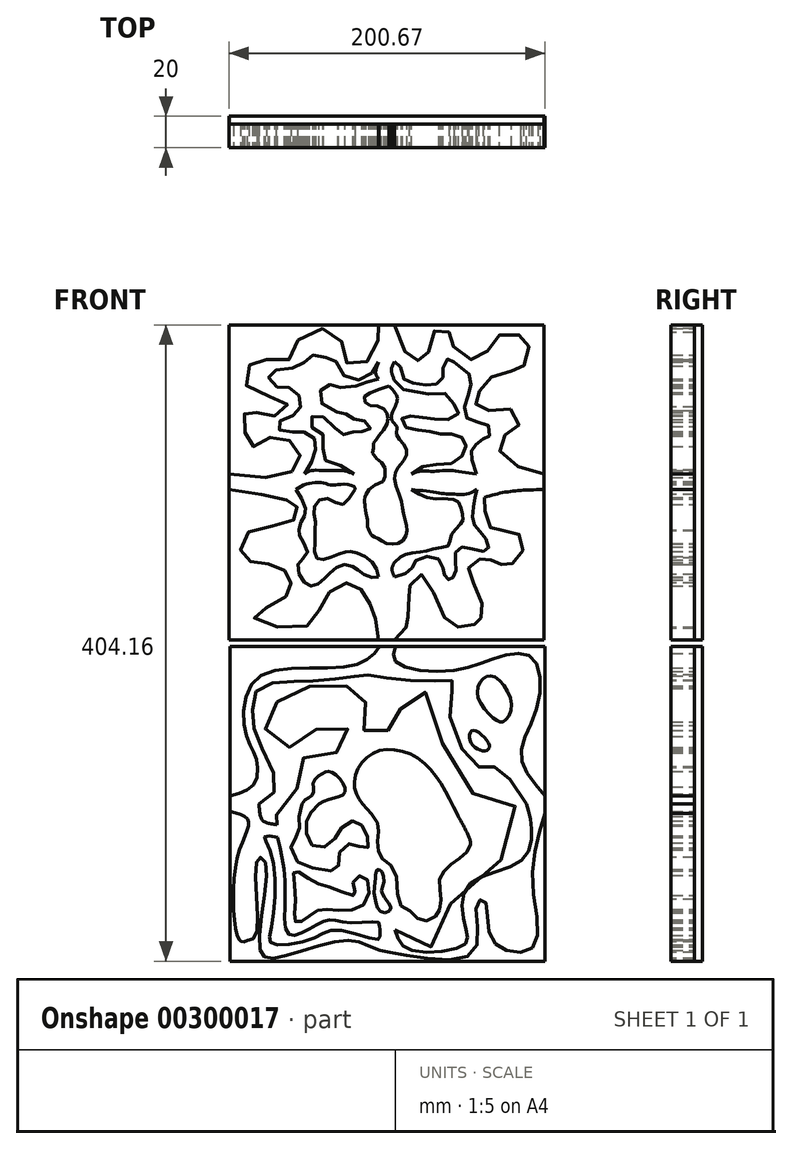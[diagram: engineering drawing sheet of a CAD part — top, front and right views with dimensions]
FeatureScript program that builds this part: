
annotation { "Feature Type Name" : "Feature", "Feature Type Description" : "" }
export const myFeature = defineFeature(function(context is Context, id is Id, definition is map)
    precondition{}
    {
        {
            var Q0;
            Q0=qCreatedBy(makeId("Front.planeOp"),FACE);
            var sketch = newSketch(context, id + "F0", { "sketchPlane" : qUnion([Q0])});
            skLineSegment(sketch, "E0", {"start": v(-68.5, 100) * mm, "end": v(-68.5, 5) * mm});
            skLineSegment(sketch, "E1", {"start": v(-33.6, 0) * mm, "end": v(31.5, 0) * mm});
            skLineSegment(sketch, "E2.MirrorCS", {"start": v(-33.6, 0) * mm, "end": v(-33.6, -5) * mm});
            skLineSegment(sketch, "E3.trimOffspring", {"start": v(-68.5, -5) * mm, "end": v(-68.5, -100) * mm});
            skPoint(sketch, "E4.orphan", {"position": v(-68.5, 0) * mm});
            skPoint(sketch, "E5.end.orphan", {"position": v(-33.6, 5) * mm});
            skPoint(sketch, "E5.start.orphan", {"position": v(-33.6, 0) * mm});
            skPoint(sketch, "E6.orphan", {"position": v(131.5, 0) * mm});
            skLineSegment(sketch, "E7.MirrorCS", {"start": v(131.5, 100) * mm, "end": v(131.5, 5) * mm});
            skLineSegment(sketch, "E8.MirrorCS", {"start": v(131.5, -6.17) * mm, "end": v(131.5, -101.16) * mm});
            skFitSpline(sketch, "E9", {"points": [v(-68.5, -5) * mm, v(-56.9, -10.75) * mm, v(-63.65, -33.28) * mm, v(-62.81, -86.22) * mm, v(-57.46, -86.78) * mm], "startDerivative": vector(80.53, -15.15) * mm, "endDerivative": vector(58.49, 27.23) * mm});
            skFitSpline(sketch, "E10", {"points": [v(-57.46, -86.78) * mm, v(-51.83, -82.56) * mm, v(-50.98, -34.96) * mm, v(-46.2, -36.94) * mm, v(-49.57, -92.42) * mm, v(-38.6, -97.77) * mm, v(5.06, -86.78) * mm, v(26.6, -93.16) * mm], "startDerivative": vector(88.86, 11.23) * mm, "endDerivative": vector(182.3, -63.3) * mm});
            skFitSpline(sketch, "E11", {"points": [v(26.6, -93.16) * mm, v(50.85, -97.41) * mm, v(87.45, -92.35) * mm, v(88.43, -62.85) * mm, v(93.18, -61.47) * mm, v(96.03, -81.43) * mm, v(108.14, -93.53) * mm, v(125.01, -89.87) * mm, v(123.62, -49.6) * mm, v(131.5, -6.17) * mm], "startDerivative": vector(93.77, -18.16) * mm, "endDerivative": vector(84.11, 264.75) * mm});
            skPoint(sketch, "E12.orphan", {"position": v(131.5, 101.16) * mm});
            skPoint(sketch, "E13.start.orphan", {"position": v(31.5, 100.58) * mm});
            skPoint(sketch, "E14.MirrorCS.end.orphan", {"position": v(31.5, -201.16) * mm});
            skPoint(sketch, "E14.MirrorCS.start.orphan", {"position": v(-33.6, -201.16) * mm});
            skLineSegment(sketch, "E15", {"start": v(-68.5, 100) * mm, "end": v(26.5, 100) * mm});
            skLineSegment(sketch, "E16", {"start": v(131.5, 100) * mm, "end": v(36.5, 100) * mm});
            skFitSpline(sketch, "E17", {"points": [v(-68.5, 5) * mm, v(-53.5, 12.19) * mm, v(-52.02, 28.9) * mm, v(-58.28, 43.81) * mm, v(-51.12, 79.92) * mm, v(7.66, 87.37) * mm, v(26.5, 100) * mm], "startDerivative": vector(131.47, 41.7) * mm, "endDerivative": vector(63, 102.47) * mm});
            skFitSpline(sketch, "E18", {"points": [v(36.5, 100) * mm, v(36.5, 90.36) * mm, v(71.2, 84.4) * mm, v(100.75, 92.74) * mm, v(123.12, 93.04) * mm, v(126.4, 61.12) * mm, v(116.26, 30.39) * mm, v(131.5, 5) * mm], "startDerivative": vector(-36.62, -111.2) * mm, "endDerivative": vector(143.7, -169.43) * mm});
            skFitSpline(sketch, "E19", {"points": [v(-50.1, 0) * mm, v(-39.36, 11.13) * mm, v(-50.1, 38.63) * mm, v(-54.21, 56.33) * mm, v(-51.05, 72.45) * mm, v(-32.08, 77.5) * mm, v(-13.43, 78.14) * mm, v(8.7, 80.67) * mm, v(18.04, 81.83) * mm, v(36.5, 79.09) * mm, v(64.96, 78.14) * mm, v(73.5, 77.5) * mm, v(70.65, 62.33) * mm, v(88.35, 23.77) * mm, v(100.36, 23.14) * mm, v(119.65, 0) * mm], "startDerivative": vector(256.93, 149.04) * mm, "endDerivative": vector(237.27, -390.24) * mm});
            skFitSpline(sketch, "E20", {"points": [v(119.65, 0) * mm, v(122.67, -12.95) * mm, v(116.9, -35.78) * mm, v(82.78, -51.84) * mm, v(81.02, -78.94) * mm, v(80.52, -89.22) * mm, v(45.14, -92.48) * mm, v(36.36, -80.2) * mm], "startDerivative": vector(32.09, -102.65) * mm, "endDerivative": vector(-34.37, 125.86) * mm});
            skFitSpline(sketch, "E21", {"points": [v(-50.1, 0) * mm, v(-47.69, -10.75) * mm, v(-38.66, -13.3) * mm], "startDerivative": vector(1.1, -24.27) * mm, "endDerivative": vector(22, -4.45) * mm});
            skFitSpline(sketch, "E22", {"points": [v(-38.4, -21.23) * mm, v(-46.43, -20.98) * mm, v(-41.67, -33.78) * mm, v(-42.67, -80.2) * mm, v(-41.92, -88.72) * mm, v(-15.57, -85.46) * mm, v(0, -80.2) * mm, v(26.5, -85.96) * mm, v(26.58, -80.2) * mm], "startDerivative": vector(-126.45, 23) * mm, "endDerivative": vector(39.4, 95.48) * mm});
            skFitSpline(sketch, "E23", {"points": [v(26.58, -80.2) * mm, v(26.5, -75.87) * mm, v(7.13, -75.58) * mm, v(-5.7, -73.79) * mm, v(-19.12, -80.2) * mm, v(-31.36, -82.74) * mm, v(-33.45, -53.8) * mm, v(-38.4, -21.23) * mm], "startDerivative": vector(-44.26, 59.3) * mm, "endDerivative": vector(-36.17, 149.66) * mm});
            skFitSpline(sketch, "E24", {"points": [v(-12.86, -67.82) * mm, v(-22.1, -74.38) * mm, v(-27.18, -74.68) * mm, v(-26.88, -60.66) * mm, v(-27.48, -42.76) * mm, v(-17.33, -48.42) * mm, v(-3.01, -53.8) * mm, v(11.01, -57.97) * mm, v(9.52, -50.21) * mm, v(16.68, -46.04) * mm, v(17.87, -62.45) * mm, v(0, -67.82) * mm, v(-12.86, -67.82) * mm]});
            skFitSpline(sketch, "E25", {"points": [v(92.17, 79.28) * mm, v(100.22, 80.17) * mm, v(110.37, 62.27) * mm, v(105, 52.12) * mm, v(99.92, 53.62) * mm, v(88.88, 67.94) * mm, v(92.17, 79.28) * mm]});
            skFitSpline(sketch, "E26", {"points": [v(93.36, 33.63) * mm, v(84.26, 39.3) * mm, v(85.6, 46.46) * mm, v(96.05, 37.5) * mm, v(93.36, 33.63) * mm]});
            skFitSpline(sketch, "E27", {"points": [v(-38.66, -13.3) * mm, v(-33.46, -13.3) * mm, v(-31.83, -8.37) * mm, v(-38.66, -8.02) * mm, v(-38.66, -5) * mm, v(-35.99, 5) * mm, v(-28.3, 9.03) * mm, v(-23.95, 10.94) * mm, v(-22.59, 18.28) * mm, v(-23.68, 27.25) * mm, v(-18.78, 30.5) * mm, v(-12.26, 32.96) * mm, v(-4.1, 32.96) * mm, v(2.7, 32.68) * mm, v(10.58, 38.94) * mm, v(8.13, 46) * mm, v(0, 49.54) * mm, v(-5.73, 49.54) * mm, v(-12.26, 48.18) * mm, v(-15.8, 46) * mm, v(-21.5, 41.93) * mm, v(-27.48, 36.22) * mm, v(-33.6, 36.57) * mm, v(-38.66, 39.01) * mm, v(-44.07, 42.47) * mm, v(-46.2, 48.73) * mm, v(-46.2, 52.53) * mm, v(-46.2, 58.51) * mm, v(-38.66, 64.57) * mm, v(-35.99, 66.7) * mm, v(-30.47, 72.92) * mm, v(-16.6, 74.28) * mm, v(-6, 73.2) * mm, v(0, 74.55) * mm, v(8.4, 74.55) * mm, v(14.66, 73.2) * mm, v(16.83, 71.02) * mm, v(17.65, 65.3) * mm, v(16.02, 59.33) * mm, v(15.2, 54.98) * mm, v(15.47, 50.9) * mm, v(17.1, 45.2) * mm, v(18.2, 43.02) * mm, v(22.81, 43.29) * mm, v(28.52, 45.2) * mm, v(35.05, 48.18) * mm, v(37.77, 49.54) * mm, v(41.03, 54.98) * mm, v(39.94, 59.87) * mm, v(37.77, 69.12) * mm, v(49.73, 73.2) * mm, v(62.5, 62.32) * mm, v(65.77, 43.02) * mm, v(71.2, 20.45) * mm, v(87.25, 6.31) * mm, v(104.92, 10.5) * mm, v(114.16, -8.1) * mm, v(113.34, -31.24) * mm, v(81.27, -42.62) * mm, v(71.75, -68.72) * mm, v(72.3, -84.76) * mm, v(53.54, -89.93) * mm, v(47.28, -80.2) * mm, v(36.36, -80.2) * mm], "startDerivative": vector(449.07, -156.16) * mm, "endDerivative": vector(-726.71, -177.94) * mm});
            skFitSpline(sketch, "E28", {"points": [v(38.85, -63.01) * mm, v(46.2, -68.45) * mm, v(53, -74.43) * mm, v(61.7, -71.71) * mm, v(64.41, -67.64) * mm, v(65.5, -58.94) * mm, v(64.14, -49.42) * mm, v(67.4, -42.62) * mm, v(73.93, -36.94) * mm, v(81.27, -31.24) * mm, v(84.26, -25.77) * mm, v(75.83, -6.74) * mm, v(52.67, 27.6) * mm, v(21.71, 31.88) * mm, v(10.51, 10.5) * mm, v(20.1, -5) * mm, v(25.5, -13.3) * mm, v(25.5, -20.14) * mm, v(25.5, -29.38) * mm, v(28.25, -34.96) * mm, v(36.36, -42.62) * mm, v(38.85, -63.01) * mm]});
            skFitSpline(sketch, "E29", {"points": [v(75.83, -6.74) * mm, v(70.65, -10.81) * mm, v(63.05, -12.72) * mm, v(53.8, -6.74) * mm, v(53.08, 19.25) * mm, v(22.9, 15.63) * mm, v(28.25, -6.16) * mm, v(28.64, -17.61) * mm, v(28.52, -27.67) * mm, v(36.68, -33.65) * mm, v(39.94, -38.82) * mm, v(42.12, -49.42) * mm, v(47.28, -59.2) * mm, v(57.61, -56.22) * mm, v(56.53, -45.34) * mm, v(63.05, -32.84) * mm, v(70.65, -27.13) * mm, v(84.26, -25.77) * mm], "startDerivative": vector(-74.58, -149.26) * mm, "endDerivative": vector(27.1, -181.26) * mm});
            skLineSegment(sketch, "E30.MirrorCS", {"start": v(-68.5, -100) * mm, "end": v(26.5, -100) * mm});
            skLineSegment(sketch, "E31.MirrorCS", {"start": v(131.5, -100) * mm, "end": v(36.5, -100) * mm});
            skFitSpline(sketch, "E32", {"points": [v(-29.51, -24.3) * mm, v(-26.44, -36.23) * mm, v(-13.17, -41.42) * mm, v(0, -41.8) * mm, v(0, -34.11) * mm, v(5.1, -26.62) * mm, v(11.05, -25.27) * mm, v(17.01, -29.3) * mm, v(20.09, -24.3) * mm, v(17.01, -18.35) * mm, v(13.17, -11.24) * mm, v(5.28, -12.78) * mm, v(0, -18.54) * mm, v(-5.48, -26.04) * mm, v(-14.7, -27.39) * mm, v(-19.7, -20.27) * mm, v(-20.1, -12.2) * mm, v(-17.98, -6.82) * mm, v(-14.32, -1.63) * mm, v(-3.75, 3.37) * mm, v(4.13, 6.64) * mm, v(2.6, 14.14) * mm, v(-5.29, 20.48) * mm, v(-9.52, 19.33) * mm, v(-15.48, 13.95) * mm, v(-15.86, 6.26) * mm, v(-21.44, 1.84) * mm, v(-24.51, -7.2) * mm, v(-24.51, -13.74) * mm, v(-25.09, -19.5) * mm, v(-29.51, -24.3) * mm]});
            skFitSpline(sketch, "E33", {"points": [v(29.85, -69.19) * mm, v(25.6, -67) * mm, v(23.66, -60.93) * mm, v(23, -55.5) * mm, v(23.78, -48.8) * mm, v(23.78, -46.47) * mm, v(24.43, -42.6) * mm, v(25.98, -41.82) * mm, v(28.56, -44.53) * mm, v(28.95, -50.47) * mm, v(27.66, -55.5) * mm, v(28.56, -57.7) * mm, v(30.5, -60.54) * mm, v(31.92, -62.6) * mm, v(33.6, -66.73) * mm, v(29.85, -69.19) * mm]});
            skLineSegment(sketch, "E34", {"start": v(26.5, -100) * mm, "end": v(36.5, -100) * mm});
            skSolve(sketch);
        }
        {
            var Q0;
            Q0 = qSketchRegion(id + "F0", true);
            extrude(context, id + "F1", {"entities" : qUnion([Q0]), "depth" : 15 * mm});
        }
        {
            var Q0;
            Q0=makeQuery(id+"F1.opExtrude","CAP_FACE",FACE,{"disambiguationData":[OSD([sQuery(id+"F0.wireOp",EDGE,"E3.trimOffspring"),sQuery(id+"F0.wireOp",EDGE,"E9"),sQuery(id+"F0.wireOp",EDGE,"E10"),sQuery(id+"F0.wireOp",EDGE,"E30.MirrorCS")])],"isStart":true});
            var sketch = newSketch(context, id + "F2", { "sketchPlane" : qUnion([Q0])});
            skLineSegment(sketch, "E35", {"start": v(68.5, -100) * mm, "end": v(-131.5, -100) * mm});
            skLineSegment(sketch, "E36", {"start": v(68.5, -100) * mm, "end": v(68.5, 100) * mm});
            skLineSegment(sketch, "E37", {"start": v(-131.5, 100) * mm, "end": v(68.5, 100) * mm});
            skLineSegment(sketch, "E38", {"start": v(-131.5, 100) * mm, "end": v(-131.5, -100) * mm});
            skSolve(sketch);
        }
        {
            var Q0;
            Q0 = qSketchRegion(id + "F2", true);
            extrude(context, id + "F3", {"entities" : qUnion([Q0]), "depth" : 5 * mm});
        }
        {
            var Q0;
            Q0=qCreatedBy(makeId("Front.planeOp"),FACE);
            var sketch = newSketch(context, id + "F4", { "sketchPlane" : qUnion([Q0])});
            skLineSegment(sketch, "E39", {"start": v(-69.17, 104.16) * mm, "end": v(25.83, 104.16) * mm});
            skLineSegment(sketch, "E40", {"start": v(-69.17, 104.16) * mm, "end": v(-69.17, 199.52) * mm});
            skLineSegment(sketch, "E41", {"start": v(-69.17, 304.16) * mm, "end": v(25.83, 304.16) * mm});
            skLineSegment(sketch, "E42", {"start": v(130.83, 304.16) * mm, "end": v(130.83, 209.52) * mm});
            skLineSegment(sketch, "E43.trimOffspring", {"start": v(35.83, 104.16) * mm, "end": v(130.83, 104.16) * mm});
            skLineSegment(sketch, "E44", {"start": v(25.83, 104.16) * mm, "end": v(25.83, 304.16) * mm, "construction": true});
            skLineSegment(sketch, "E45", {"start": v(35.83, 104.16) * mm, "end": v(35.83, 304.16) * mm, "construction": true});
            skLineSegment(sketch, "E46.trimOffspring", {"start": v(35.83, 304.16) * mm, "end": v(130.83, 304.16) * mm});
            skLineSegment(sketch, "E47", {"start": v(117.02, 209.52) * mm, "end": v(-69.17, 209.52) * mm, "construction": true});
            skLineSegment(sketch, "E48", {"start": v(-69.14, 199.52) * mm, "end": v(-69.17, 199.52) * mm, "construction": true});
            skLineSegment(sketch, "E49", {"start": v(117.02, 209.52) * mm, "end": v(130.83, 209.52) * mm, "construction": true});
            skLineSegment(sketch, "E50", {"start": v(-69.14, 199.52) * mm, "end": v(130.83, 199.52) * mm, "construction": true});
            skLineSegment(sketch, "E51.trimOffspring", {"start": v(130.83, 199.52) * mm, "end": v(130.83, 104.16) * mm});
            skLineSegment(sketch, "E52.trimOffspring", {"start": v(-69.17, 209.52) * mm, "end": v(-69.17, 304.16) * mm});
            skFitSpline(sketch, "E53", {"points": [v(-69.17, 209.52) * mm, v(-31.92, 209.52) * mm, v(-23.98, 219.55) * mm, v(-28.56, 229.01) * mm, v(-41.68, 233.29) * mm, v(-53.28, 226.88) * mm, v(-58.16, 232.98) * mm, v(-60, 246.4) * mm, v(-55.72, 249.76) * mm, v(-46.57, 246.71) * mm, v(-35.27, 248.54) * mm, v(-32.83, 255.87) * mm, v(-55.72, 262.28) * mm, v(-57.25, 276.62) * mm, v(-49, 282.42) * mm, v(-31, 282.1) * mm, v(-23.37, 297.06) * mm, v(0, 298.59) * mm, v(5, 280.89) * mm, v(17.82, 280.28) * mm, v(25.83, 296.76) * mm, v(25.83, 304.16) * mm], "startDerivative": vector(556.56, -70.96) * mm, "endDerivative": vector(-19.04, 186.24) * mm});
            skFitSpline(sketch, "E54", {"points": [v(-69.17, 199.52) * mm, v(-30.7, 192.4) * mm, v(-25.8, 187.82) * mm, v(-29.78, 178.96) * mm, v(-57.25, 172.26) * mm, v(-60.3, 156.69) * mm, v(-47.48, 152.73) * mm, v(-33.44, 147.85) * mm, v(-29.77, 139) * mm, v(-36.5, 128.92) * mm, v(-53.29, 118.55) * mm, v(-20.93, 112.44) * mm, v(-9.64, 128.62) * mm, v(5, 140.22) * mm, v(16.3, 134.42) * mm, v(22.1, 121.9) * mm, v(25.83, 104.16) * mm], "startDerivative": vector(491.94, -68.6) * mm, "endDerivative": vector(0, -420.31) * mm});
            skFitSpline(sketch, "E55", {"points": [v(35.83, 104.16) * mm, v(43.84, 112.9) * mm, v(44.53, 116.79) * mm, v(45.21, 133.7) * mm, v(45.44, 137.6) * mm, v(52.76, 145.6) * mm, v(65.56, 122.27) * mm, v(75.85, 112.22) * mm, v(87.5, 114.27) * mm, v(90.02, 116.79) * mm, v(92.08, 122.73) * mm, v(85.45, 141.48) * mm, v(83.4, 150.62) * mm, v(92.08, 156.1) * mm, v(96.65, 155.2) * mm, v(102.6, 152.45) * mm, v(106.7, 151.76) * mm, v(114.7, 155.42) * mm, v(117, 168.91) * mm, v(106.25, 173.48) * mm, v(97.56, 174.4) * mm, v(93.45, 186.28) * mm, v(93.11, 194.5) * mm], "startDerivative": vector(206.24, 202) * mm, "endDerivative": vector(124.12, 183.85) * mm});
            skFitSpline(sketch, "E56", {"points": [v(93.11, 194.5) * mm, v(130.83, 199.52) * mm], "startDerivative": vector(37.67, 13.47) * mm, "endDerivative": vector(37.38, 0) * mm});
            skFitSpline(sketch, "E57", {"points": [v(130.83, 209.52) * mm, v(112.14, 215.44) * mm, v(102.36, 225.5) * mm, v(105.35, 233.38) * mm, v(111.05, 237.18) * mm, v(115.95, 243.98) * mm, v(105.89, 251.86) * mm, v(93.93, 249.42) * mm, v(87.95, 252.4) * mm, v(88.22, 257.3) * mm, v(90.12, 262.47) * mm, v(95.01, 269.54) * mm, v(106.43, 273.89) * mm, v(114.59, 276.06) * mm, v(118.12, 278.23) * mm, v(121.39, 288.57) * mm, v(120.03, 294.27) * mm, v(111.87, 298.9) * mm, v(101.54, 297) * mm, v(95.29, 287.75) * mm, v(87.95, 282.04) * mm, v(74.63, 287.48) * mm, v(72.45, 297) * mm, v(69.73, 300.26) * mm, v(63.2, 301.61) * mm, v(58.04, 293.19) * mm, v(55.87, 281.5) * mm, v(48.8, 282.04) * mm, v(43.63, 285.57) * mm, v(35.83, 304.16) * mm], "startDerivative": vector(-388.5, 86.83) * mm, "endDerivative": vector(-152.5, 444.13) * mm});
            skFitSpline(sketch, "E58", {"points": [v(-26.72, 199.52) * mm, v(-20.9, 188.77) * mm, v(-21.33, 182.3) * mm, v(-24.13, 177.33) * mm, v(-24.57, 171.5) * mm, v(-23.27, 168.49) * mm, v(-19.39, 158.56) * mm, v(-24.57, 154.03) * mm, v(-24.35, 145.4) * mm, v(-18.3, 138.5) * mm, v(-13.56, 139.14) * mm, v(-7.73, 143.89) * mm, v(-2.77, 148.63) * mm, v(4.13, 151.87) * mm, v(10.82, 149.93) * mm, v(13.84, 147.56) * mm, v(20.96, 143.89) * mm, v(25.83, 144.1) * mm], "startDerivative": vector(61.4, -85.94) * mm, "endDerivative": vector(88.58, 19.02) * mm});
            skFitSpline(sketch, "E59", {"points": [v(35.83, 144.1) * mm, v(46.2, 148.42) * mm, v(49.45, 154.46) * mm, v(62.82, 156.19) * mm, v(66.92, 148.2) * mm, v(68.22, 144.1) * mm, v(71.02, 142.16) * mm, v(73.4, 144.1) * mm, v(75.12, 150.14) * mm, v(74.48, 158.78) * mm, v(79.44, 163.1) * mm, v(91.95, 160.29) * mm, v(95.62, 162.44) * mm, v(92.82, 170) * mm, v(87.42, 176.04) * mm, v(85.48, 182.94) * mm, v(86.77, 192.87) * mm, v(88.28, 199.52) * mm], "startDerivative": vector(177.35, 42.78) * mm, "endDerivative": vector(25.93, 109.48) * mm});
            skFitSpline(sketch, "E60", {"points": [v(87.85, 209.52) * mm, v(84.62, 220.7) * mm, v(84.83, 224.59) * mm, v(87, 227.6) * mm, v(90.87, 231.28) * mm, v(94.76, 231.92) * mm, v(96.48, 235.38) * mm, v(94.11, 241.85) * mm, v(84.62, 242.93) * mm, v(80.52, 248.54) * mm, v(81.6, 256.52) * mm, v(84.4, 264.72) * mm, v(83.75, 272.49) * mm, v(79.65, 275.94) * mm, v(74.9, 279.4) * mm, v(71.02, 282.41) * mm, v(69.08, 281.98) * mm, v(66.7, 275.73) * mm, v(66.7, 270.76) * mm, v(63.04, 266.88) * mm, v(57, 266.02) * mm, v(46.64, 267.3) * mm, v(41.68, 270.12) * mm, v(39.09, 278.75) * mm, v(35.83, 280.9) * mm], "startDerivative": vector(-72.03, 216.62) * mm, "endDerivative": vector(-110.9, 35.66) * mm});
            skFitSpline(sketch, "E61", {"points": [v(25.83, 280.47) * mm, v(22.47, 274.43) * mm, v(16.22, 270.12) * mm, v(5.43, 270.12) * mm, v(0, 279.82) * mm, v(-5.36, 283.06) * mm, v(-9.46, 283.7) * mm, v(-17.01, 284.79) * mm, v(-21.11, 280.9) * mm, v(-26.3, 277.24) * mm, v(-36.22, 275.94) * mm, v(-43.77, 273.35) * mm, v(-42.7, 268.17) * mm, v(-37.51, 264.5) * mm, v(-31.47, 264.5) * mm, v(-26.72, 261.05) * mm, v(-22.84, 255.66) * mm, v(-25.43, 249.62) * mm, v(-28.45, 246.71) * mm, v(-36, 243.57) * mm, v(-39.24, 239.04) * mm, v(-31.9, 236.24) * mm, v(-27.15, 236.24) * mm, v(-21.98, 236.24) * mm, v(-15.72, 233) * mm, v(-14.2, 229.33) * mm, v(-14.42, 222.86) * mm, v(-17.23, 216.17) * mm, v(-21.33, 209.52) * mm], "startDerivative": vector(-80.5, -176.67) * mm, "endDerivative": vector(-109.85, -171.25) * mm});
            skFitSpline(sketch, "E62", {"points": [v(25.83, 144.1) * mm, v(22.15, 153.25) * mm, v(12.22, 159.3) * mm, v(6.9, 160.27) * mm, v(2.05, 159.3) * mm, v(-7.4, 155.43) * mm, v(-13.7, 156.16) * mm, v(-14.67, 166.68) * mm, v(-14.67, 172.72) * mm, v(-14.46, 180.06) * mm, v(-14.89, 189.34) * mm, v(-7.12, 194.09) * mm, v(2.53, 190.06) * mm, v(10.77, 199.52) * mm], "startDerivative": vector(-24.4, 113.1) * mm, "endDerivative": vector(87.6, 111.83) * mm});
            skFitSpline(sketch, "E63", {"points": [v(10.35, 209.52) * mm, v(2, 214.88) * mm, v(-7.61, 217.97) * mm, v(-9.43, 223.05) * mm, v(-9.25, 229.94) * mm, v(-10.7, 236.66) * mm, v(-17.23, 239.56) * mm, v(-17.05, 245.36) * mm, v(-13.24, 246.82) * mm, v(-5.98, 243.37) * mm, v(0, 236.3) * mm, v(3.27, 234.48) * mm, v(5.81, 235.2) * mm, v(10.35, 236.3) * mm, v(13.8, 236.47) * mm, v(16.34, 236.3) * mm, v(19.6, 237.56) * mm, v(20.87, 239.74) * mm, v(17.25, 243) * mm, v(12.9, 243.55) * mm, v(8.17, 245.18) * mm, v(5.63, 247.18) * mm, v(3.46, 248.45) * mm, v(0, 248.63) * mm, v(-9.97, 253.9) * mm, v(-11.79, 261.15) * mm, v(-8.34, 264.96) * mm, v(-3.98, 266.23) * mm, v(0, 264.78) * mm, v(9.62, 264.78) * mm, v(15.8, 267.14) * mm, v(20.15, 268.23) * mm, v(25.83, 269.86) * mm], "startDerivative": vector(-176.36, 147.71) * mm, "endDerivative": vector(179.34, 55.88) * mm});
            skFitSpline(sketch, "E64", {"points": [v(35.83, 268.9) * mm, v(39.23, 264.1) * mm, v(43.68, 262.91) * mm, v(50.02, 261.54) * mm, v(52.93, 261.2) * mm, v(57.55, 260.34) * mm, v(66.7, 261.03) * mm, v(70.91, 257.94) * mm, v(74.17, 252.98) * mm, v(75.7, 250.07) * mm, v(76.4, 247.5) * mm, v(72.8, 244.59) * mm, v(66.7, 244.24) * mm, v(61.66, 244.41) * mm, v(57.04, 244.93) * mm, v(53.27, 245.27) * mm, v(47.96, 246.13) * mm, v(44.54, 246.64) * mm, v(41.8, 246.64) * mm, v(40.26, 242.36) * mm, v(41.8, 239.62) * mm, v(45.05, 238.42) * mm, v(49.5, 237.56) * mm, v(55.67, 236.7) * mm, v(58.58, 236.54) * mm, v(62.52, 236.02) * mm, v(65.09, 234.82) * mm, v(69.88, 235) * mm, v(72.62, 234.82) * mm, v(77.08, 234.14) * mm, v(79.13, 232.43) * mm, v(80.5, 231.06) * mm, v(81.19, 226.95) * mm, v(80.84, 223.35) * mm, v(78.45, 220.27) * mm, v(74.34, 216.67) * mm, v(68, 215.81) * mm, v(61.83, 215.47) * mm, v(58.4, 214.79) * mm, v(48.48, 212.56) * mm, v(46.64, 209.52) * mm], "startDerivative": vector(105.86, -200.4) * mm, "endDerivative": vector(-36.44, -149.86) * mm});
            skFitSpline(sketch, "E65", {"points": [v(46.64, 199.52) * mm, v(53.37, 195.67) * mm, v(61.35, 193.73) * mm, v(66.7, 193.94) * mm, v(68.9, 193.73) * mm, v(72.14, 193.51) * mm, v(75.38, 192.43) * mm, v(77.54, 190.06) * mm, v(78.83, 185.31) * mm, v(79.26, 182.5) * mm, v(79.05, 179.27) * mm, v(77.54, 177.33) * mm, v(73.65, 173.01) * mm, v(71.5, 169.78) * mm, v(70.85, 165.46) * mm, v(69.77, 163.74) * mm, v(64.37, 162.66) * mm, v(57.9, 161.15) * mm, v(54.45, 160.28) * mm, v(48.48, 159.42) * mm, v(43.23, 158.56) * mm, v(40.64, 157.48) * mm, v(35.83, 153.38) * mm], "startDerivative": vector(105.6, -68.8) * mm, "endDerivative": vector(-95.03, -88.09) * mm});
            skFitSpline(sketch, "E66", {"points": [v(46.64, 209.52) * mm, v(53.58, 211.3) * mm, v(59.72, 211.15) * mm, v(67.97, 211.8) * mm, v(75.24, 211.3) * mm, v(87.85, 209.52) * mm], "startDerivative": vector(38, 12.85) * mm, "endDerivative": vector(54.49, -7.96) * mm});
            skFitSpline(sketch, "E67", {"points": [v(46.64, 199.52) * mm, v(60.2, 198.12) * mm, v(68.13, 196.92) * mm, v(74.75, 196.6) * mm, v(80.74, 196.44) * mm, v(88.28, 199.52) * mm], "startDerivative": vector(56.48, -4.8) * mm, "endDerivative": vector(39.02, 20.28) * mm});
            skFitSpline(sketch, "E68", {"points": [v(25.83, 269.86) * mm, v(23.97, 273.76) * mm, v(25.83, 280.47) * mm], "startDerivative": vector(-5.87, 8.15) * mm, "endDerivative": vector(5.42, 12.88) * mm});
            skFitSpline(sketch, "E69", {"points": [v(35.83, 280.9) * mm, v(33.95, 276.11) * mm, v(34.14, 273.76) * mm, v(35.83, 268.9) * mm], "startDerivative": vector(-6.56, -14.15) * mm, "endDerivative": vector(5.36, -14.36) * mm});
            skFitSpline(sketch, "E70", {"points": [v(10.35, 209.52) * mm, v(3.27, 211.61) * mm, v(-3.42, 211.61) * mm, v(-8.69, 211.61) * mm, v(-16.67, 211.61) * mm, v(-21.33, 209.52) * mm], "startDerivative": vector(-32.63, 12.4) * mm, "endDerivative": vector(-23.26, -14.55) * mm});
            skFitSpline(sketch, "E71", {"points": [v(-26.72, 199.52) * mm, v(-21.33, 202.63) * mm, v(-15.76, 203.9) * mm, v(-9.97, 204.08) * mm, v(-5.98, 202.81) * mm, v(-1.8, 202.45) * mm, v(3.27, 203) * mm, v(10.35, 201.36) * mm, v(10.77, 199.52) * mm], "startDerivative": vector(37.76, 25.26) * mm, "endDerivative": vector(-2.62, -25.3) * mm});
            skFitSpline(sketch, "E72", {"points": [v(35.83, 153.38) * mm, v(34.46, 150) * mm, v(34.35, 148.2) * mm, v(35.83, 144.1) * mm], "startDerivative": vector(-4.6, -10.36) * mm, "endDerivative": vector(4.9, -11.7) * mm});
            skFitSpline(sketch, "E73", {"points": [v(32.35, 265.37) * mm, v(20.2, 260.84) * mm, v(16.75, 258.12) * mm, v(18.38, 253.94) * mm, v(24, 252.67) * mm, v(29.8, 250.31) * mm, v(31.44, 247.18) * mm, v(31.62, 243.55) * mm, v(29.8, 238.52) * mm, v(25.83, 233.8) * mm, v(23.82, 230.9) * mm, v(22.55, 229.27) * mm, v(22.55, 226) * mm, v(21.83, 222.91) * mm, v(25.83, 218.02) * mm, v(29.26, 214.93) * mm, v(29.8, 207.13) * mm, v(27.63, 204.23) * mm, v(19.72, 199.52) * mm], "startDerivative": vector(-153.06, -54.37) * mm, "endDerivative": vector(-2.9, -79.32) * mm});
            skFitSpline(sketch, "E74", {"points": [v(30.81, 165.46) * mm, v(38.52, 165.46) * mm, v(43.24, 170.3) * mm, v(43.78, 176.28) * mm, v(41.6, 184.09) * mm, v(40.33, 192.8) * mm, v(35.83, 206.95) * mm, v(38.16, 213.48) * mm, v(41.42, 217.47) * mm, v(43.78, 223.46) * mm, v(39.79, 230.72) * mm, v(37.61, 239.62) * mm], "startDerivative": vector(94.76, -15.33) * mm, "endDerivative": vector(54.47, 150.06) * mm});
            skFitSpline(sketch, "E75", {"points": [v(37.61, 239.62) * mm, v(33.98, 244.69) * mm, v(35.83, 251.4) * mm, v(37.61, 258.12) * mm, v(32.35, 265.37) * mm], "startDerivative": vector(-21.29, 20.44) * mm, "endDerivative": vector(-25.88, 25.82) * mm});
            skFitSpline(sketch, "E76", {"points": [v(19.72, 199.52) * mm, v(17.65, 195.77) * mm, v(16.88, 191.35) * mm, v(17.26, 189.05) * mm, v(18.03, 183.66) * mm, v(18.6, 181.36) * mm, v(18.9, 175.69) * mm, v(19.72, 173.86) * mm, v(20.92, 171.36) * mm, v(22.07, 170.2) * mm, v(30.81, 165.46) * mm], "startDerivative": vector(-21.94, -32.49) * mm, "endDerivative": vector(67.13, -34.89) * mm});
            skSolve(sketch);
        }
        {
            var Q0;
            Q0 = qSketchRegion(id + "F4", true);
            extrude(context, id + "F5", {"entities" : qUnion([Q0]), "depth" : 15 * mm});
        }
        {
            var Q0;
            Q0=makeQuery(id+"F5.opExtrude","CAP_FACE",FACE,{"disambiguationData":[OSD([sQuery(id+"F4.wireOp",EDGE,"E39"),sQuery(id+"F4.wireOp",EDGE,"E40"),sQuery(id+"F4.wireOp",EDGE,"E54")])],"isStart":true});
            var sketch = newSketch(context, id + "F6", { "sketchPlane" : qUnion([Q0])});
            skLineSegment(sketch, "E77", {"start": v(69.17, 104.16) * mm, "end": v(-130.83, 104.16) * mm});
            skLineSegment(sketch, "E78", {"start": v(69.17, 104.16) * mm, "end": v(69.17, 304.16) * mm});
            skPoint(sketch, "E78.endSnap0", {"position": v(69.17, 151.84) * mm});
            skLineSegment(sketch, "E79", {"start": v(-130.83, 104.16) * mm, "end": v(-130.83, 304.16) * mm});
            skLineSegment(sketch, "E80", {"start": v(-130.83, 304.16) * mm, "end": v(69.17, 304.16) * mm});
            skSolve(sketch);
        }
        {
            var Q0;
            Q0 = qSketchRegion(id + "F6", true);
            extrude(context, id + "F7", {"entities" : qUnion([Q0]), "depth" : 5 * mm});
        }
    });
